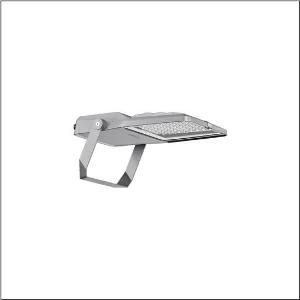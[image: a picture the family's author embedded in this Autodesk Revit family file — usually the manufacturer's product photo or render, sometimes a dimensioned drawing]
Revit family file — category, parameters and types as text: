
# Revit family: floodlight_fl_21_mini___pl43_5xa7773c4a1a_b3c2
name_source: partatom
category: Lighting Fixtures
units: mm (PartAtom-declared; Revit-internal decimal feet)

## family parameters
Cut with Voids When Loaded = No
Host = Face
Light Source = No
Part Type = Normal
Room Calculation Point = No
Round Connector Dimension = Use Diameter
Shared = No

## types (1)
- --- (1 x LED, 20890 lm, 163.5 W, 4000K)
    Apparent Load = 163 VA
    CIE Flux Codes = 27 78 99 100 100
    Color Rendering = 70
    Color Temperature = 4000K
    Default Elevation = 1800 mm
    Description = Floodlight FL 21 mini, floodlight, primary light control with lens, of PMMA, primary optical cover: protective disc, of toughened safety glass, transparent, light distribution: PL43, light emission: direct distribution, installation type: surface-mounted, LED, High Power LED, rated luminous flux: 20.890lm, luminous efficacy: 128lm/W, light colour: 740, colour temperature: 4000K, control: Temp-Guard, with terminal, 6-pole, mains connection: 220..240V, AC, 50/60Hz, start of lifetime: 164W, luminaire housing, of diecast aluminium, powder-coated, Siteco® metallic grey (DB 702S), corrosivity category C5 mid according to DIN EN ISO 12944, sealing non-destructively replaceable, mounting bracket, of steel, galvanised, powder-coated, Siteco® metallic grey (DB 702S), ON/OFF, protection rating (complete): IP66, insulation class (complete): insulation class I (protective earthing), certification: CE, ENEC, VDE, protection symbol: D, impact resistance: IK08, permissible operating ambient temperature: -40..+40°C, permissible operating ambient temperature for outdoor applications: -40..+50°C, standard: DIN EN 12944, LABS conformity tested according to VDMA 24364:2018-05, packaging unit: 1 piece

Light Distribution: PL43
    Height = 70 mm
    Lamp = 1 x LED
    Lamp Light Flux = 20890 lm
    Lamp Power = 163.5 W
    Lamp count = 1
    Length = 485 mm
    Luminous efficacy = 128 lm/W
    Manufacturer = Siteco
    ModVariant = No
    Model = 5XA7773C4A1A
    Number of Poles = 1
    OnlyDefault = Yes
    Power Factor = 1
    Product Name = Floodlight FL 21 mini | PL43
    Product group = floodlight | pylon annexe
    ProductGroupID = 6200
    Protection Class = Protection class I
    Protection Degree = IP 66
    RLX_Detail_Level = 1
    RLX_Emergency_Light_Flux = 0 lm
    RLX_Emergency_Type = 0
    RLX_Emergency_Type_DB = No
    RlxData = <blob elided: 94161 chars, md5=afafc476>
    Socket = socket
    Standby Power = 0 W
    System Light Flux = 20890 lm
    System Power = 163 W
    Type Comments = factory setting: luminous flux: 100 % | (ON | - | - | - | - | - | - | -) | 825 mA
    Type Image = l_1006845.jpg
    URL = http://relux.com
    VarID = @adj_111851
    Voltage = 0 V
    Weight = 0.00 kg
    Width = 337 mm

## geometry (parser evidence)
native form markers: Blend x4, Sweep x13
no freeform markers — native parametric forms only
